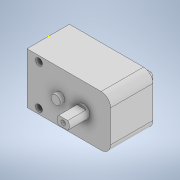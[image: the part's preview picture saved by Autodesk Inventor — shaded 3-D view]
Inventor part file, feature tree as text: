
AUTODESK INVENTOR PART (.ipt)
format: ipt  version: 2022 (Build 260153070, 153G)  size: 159,232 bytes
history: native  units: in
note: dims shown in document units (in); Inventor stores cm internally (conversion verified against a paired STEP export)
features: extrude x6, sketch x4
ambient origin geometry x8: Origin, YZ Plane, XZ Plane, XY Plane, X Axis, Y Axis, Z Axis, Center Point
bodies: Solid1 (feature_tree)
feature tree (10):
  sketch  "Sketch1"  dims[d6=0.1575in d8=0.1181in d11=0.2067in]
  extrude  "Extrusion1"  Depth=0.1181in
  extrude  "Extrusion2"  Depth=0.876in
  extrude  "Extrusion3"  Depth=0.5512in
  extrude  "Extrusion4"  Depth=0.1457in
  sketch  "Sketch2"  dims[d12=0.876in d13=0.3445in]
  extrude  "Extrusion5"  Depth=0.7283in TaperAngle=0.0deg
  extrude  "Extrusion6"  Depth=0.8858in TaperAngle=0.0deg
  sketch  "Sketch3"  dims[d16=0.5709in d17=0.5512in]
  sketch  "Sketch4"  dims[d18=1.437in d19=0.1457in d20=0.7283in d21=0.0in d22=0.8858in d23=0.0in d24=0.8071in d25=0.0in d26=1.437in d27=0.0in d28=0.2126in d29=0.4606in d30=0.0787in d31=0.1969in d32=0.0in d33=0.0787in d34=0.1969in d35=0.0in]
